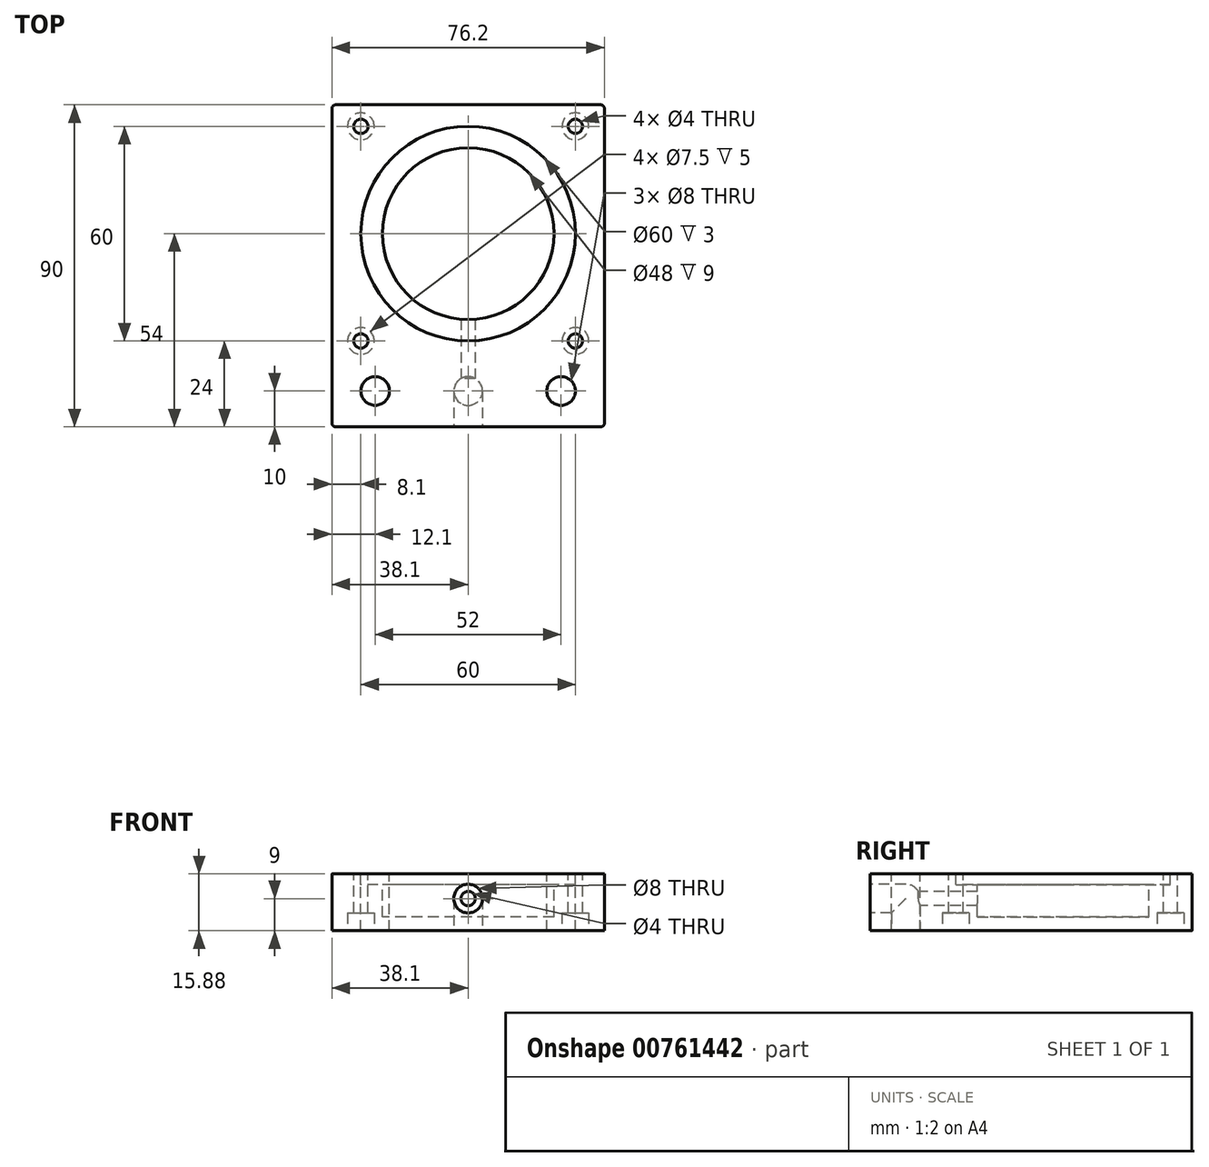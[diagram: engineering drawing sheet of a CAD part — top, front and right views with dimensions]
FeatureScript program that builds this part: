
annotation { "Feature Type Name" : "Feature", "Feature Type Description" : "" }
export const myFeature = defineFeature(function(context is Context, id is Id, definition is map)
    precondition{}
    {
        {
            var Q0;
            Q0=qCreatedBy(makeId("Top.planeOp"),FACE);
            var sketch = newSketch(context, id + "F0", { "sketchPlane" : qUnion([Q0])});
            skLineSegment(sketch, "E0.bottom", {"start": v(0, 0) * mm, "end": v(76.2, 0) * mm});
            skLineSegment(sketch, "E0.top", {"start": v(0, 90) * mm, "end": v(76.2, 90) * mm});
            skLineSegment(sketch, "E0.left", {"start": v(0, 0) * mm, "end": v(0, 90) * mm});
            skLineSegment(sketch, "E0.right", {"start": v(76.2, 0) * mm, "end": v(76.2, 90) * mm});
            skSolve(sketch);
        }
        {
            var Q0;
            Q0=makeQuery(id+"F0.imprint","IMPRINT",FACE,{"disambiguationData":[TD([[makeQuery(id+"F0.imprint","IMPRINT",EDGE,{"derivedFrom":sQuery(id+"F0.wireOp",EDGE,"E0.bottom")}),1.0]])]});
            extrude(context, id + "F1", {"entities" : qUnion([Q0]), "depth" : 15.88 * mm, "offsetDistance" : 25 * mm});
        }
        {
            var Q0;
            Q0=makeQuery(id+"F1.opExtrude","CAP_FACE",FACE,{"disambiguationData":[OSD([sQuery(id+"F0.wireOp",EDGE,"E0.bottom"),sQuery(id+"F0.wireOp",EDGE,"E0.top"),sQuery(id+"F0.wireOp",EDGE,"E0.left"),sQuery(id+"F0.wireOp",EDGE,"E0.right")])],"isStart":false});
            var sketch = newSketch(context, id + "F2", { "sketchPlane" : qUnion([Q0])});
            skCircle(sketch, "E1", {"center": v(38.1, 54) * mm, "radius": 24 * mm});
            skSolve(sketch);
        }
        {
            var Q0;
            Q0=makeQuery(id+"F2.imprint","IMPRINT",FACE,{"disambiguationData":[TD([[makeQuery(id+"F2.imprint","IMPRINT",EDGE,{"derivedFrom":sQuery(id+"F2.wireOp",EDGE,"E1")}),1.0]])]});
            extrude(context, id + "F3", {"entities" : qUnion([Q0]), "operationType" : NewBodyOperationType.REMOVE, "oppositeDirection" : true, "depth" : 12 * mm, "offsetDistance" : 25 * mm});
        }
        {
            var Q0;
            Q0=makeQuery(id+"F1.opExtrude","CAP_FACE",FACE,{"disambiguationData":[OSD([sQuery(id+"F0.wireOp",EDGE,"E0.bottom"),sQuery(id+"F0.wireOp",EDGE,"E0.top"),sQuery(id+"F0.wireOp",EDGE,"E0.left"),sQuery(id+"F0.wireOp",EDGE,"E0.right")])],"isStart":false});
            var sketch = newSketch(context, id + "F4", { "sketchPlane" : qUnion([Q0])});
            skCircle(sketch, "E2", {"center": v(38.1, 54) * mm, "radius": 30 * mm});
            skSolve(sketch);
        }
        {
            var Q0;
            Q0=makeQuery(id+"F4.imprint","IMPRINT",FACE,{"disambiguationData":[TD([[makeQuery(id+"F4.imprint","IMPRINT",EDGE,{"derivedFrom":sQuery(id+"F4.wireOp",EDGE,"E2")}),1.0]])]});
            var Q1;
            Q1=sQuery(id+"F4.wireOp",EDGE,"E2");
            extrude(context, id + "F5", {"entities" : qUnion([Q0]), "operationType" : NewBodyOperationType.REMOVE, "surfaceEntities" : qUnion([Q1]), "oppositeDirection" : true, "depth" : 3 * mm, "offsetDistance" : 25 * mm});
        }
        {
            var Q0;
            Q0=makeQuery(id+"F1.opExtrude","SWEPT_FACE",FACE,{"disambiguationData":[OSD([sQuery(id+"F0.wireOp",EDGE,"E0.bottom")])]});
            var sketch = newSketch(context, id + "F6", { "sketchPlane" : qUnion([Q0])});
            skCircle(sketch, "E3", {"center": v(38.1, 9) * mm, "radius": 4 * mm});
            skSolve(sketch);
        }
        {
            var Q0;
            Q0=makeQuery(id+"F6.imprint","IMPRINT",FACE,{"disambiguationData":[TD([[makeQuery(id+"F6.imprint","IMPRINT",EDGE,{"derivedFrom":sQuery(id+"F6.wireOp",EDGE,"E3")}),1.0]])]});
            extrude(context, id + "F7", {"entities" : qUnion([Q0]), "operationType" : NewBodyOperationType.REMOVE, "oppositeDirection" : true, "depth" : 10 * mm, "offsetDistance" : 25 * mm});
        }
        {
            var Q0;
            Q0=makeQuery(id+"F1.opExtrude","CAP_FACE",FACE,{"disambiguationData":[OSD([sQuery(id+"F0.wireOp",EDGE,"E0.bottom"),sQuery(id+"F0.wireOp",EDGE,"E0.top"),sQuery(id+"F0.wireOp",EDGE,"E0.left"),sQuery(id+"F0.wireOp",EDGE,"E0.right")])],"isStart":true});
            var sketch = newSketch(context, id + "F8", { "sketchPlane" : qUnion([Q0])});
            skCircle(sketch, "E4", {"center": v(38.1, -10) * mm, "radius": 4 * mm});
            skSolve(sketch);
        }
        {
            var Q0;
            Q0=makeQuery(id+"F8.imprint","IMPRINT",FACE,{"disambiguationData":[TD([[makeQuery(id+"F8.imprint","IMPRINT",EDGE,{"derivedFrom":sQuery(id+"F8.wireOp",EDGE,"E4")}),1.0]])]});
            extrude(context, id + "F9", {"entities" : qUnion([Q0]), "operationType" : NewBodyOperationType.REMOVE, "oppositeDirection" : true, "depth" : 9 * mm, "offsetDistance" : 25 * mm});
        }
        {
            var Q0;
            Q0=makeQuery(id+"F7.boolean.opBoolean","COPY",FACE,{"derivedFrom":makeQuery(id+"F7.opExtrude","CAP_FACE",FACE,{"disambiguationData":[OSD([sQuery(id+"F6.wireOp",EDGE,"E3")])],"isStart":false})});
            var sketch = newSketch(context, id + "F10", { "sketchPlane" : qUnion([Q0])});
            skArc(sketch, "E5", {"start": v(38.1, 13) * mm, "mid": v(34.1, 9) * mm, "end": v(38.1, 5) * mm});
            skLineSegment(sketch, "E6", {"start": v(38.1, 13) * mm, "end": v(38.1, 5) * mm});
            skSolve(sketch);
        }
        {
            var Q0;
            {var subQ0=sQuery(id+"F10.wireOp",EDGE,"E5");var subQ1=sQuery(id+"F6.wireOp",EDGE,"E3");var subQ2=makeQuery(id+"F9.boolean.opBoolean","INTERSECT",EDGE,{"derivedFrom":[makeQuery(id+"F7.boolean.opBoolean","COPY",FACE,{"derivedFrom":makeQuery(id+"F7.opExtrude","CAP_FACE",FACE,{"disambiguationData":[OSD([subQ1])],"isStart":false})}),makeQuery(id+"F9.opExtrude","CAP_FACE",FACE,{"disambiguationData":[OSD([sQuery(id+"F8.wireOp",EDGE,"E4")])],"isStart":false})]});var subQ3=makeQuery(id+"F10.imprint","INTERSECT",VERTEX,{"derivedFrom":[subQ2,subQ0]});Q0=makeQuery(id+"F10.imprint","IMPRINT",FACE,{"disambiguationData":[TD([[makeQuery(id+"F10.imprint","IMPRINT",EDGE,{"disambiguationData":[TD([[subQ3,1.0]])],"derivedFrom":subQ0}),1.0]])]});}
            var Q1;
            Q1=sQuery(id+"F10.wireOp",EDGE,"E6");
            revolve(context, id + "F11", {"operationType" : NewBodyOperationType.REMOVE, "surfaceOperationType" : NewSurfaceOperationType.NEW, "entities" : qUnion([Q0]), "axis" : qUnion([Q1]), "revolveType" : RevolveType.FULL, "oppositeDirection" : true});
        }
        {
            var Q0;
            Q0=makeQuery(id+"F1.opExtrude","SWEPT_FACE",FACE,{"disambiguationData":[OSD([sQuery(id+"F0.wireOp",EDGE,"E0.bottom")])]});
            var sketch = newSketch(context, id + "F12", { "sketchPlane" : qUnion([Q0])});
            skCircle(sketch, "E7", {"center": v(38.1, 9) * mm, "radius": 2 * mm});
            skSolve(sketch);
        }
        {
            var Q0;
            Q0=makeQuery(id+"F12.imprint","IMPRINT",FACE,{"disambiguationData":[TD([[makeQuery(id+"F12.imprint","IMPRINT",EDGE,{"derivedFrom":sQuery(id+"F12.wireOp",EDGE,"E7")}),1.0]])]});
            extrude(context, id + "F13", {"entities" : qUnion([Q0]), "operationType" : NewBodyOperationType.REMOVE, "oppositeDirection" : true, "depth" : 50 * mm, "offsetDistance" : 25 * mm});
        }
        {
            var Q0;
            Q0=makeQuery(id+"F5.boolean.opBoolean","COPY",EDGE,{"derivedFrom":makeQuery(id+"F5.opExtrude","CAP_EDGE",EDGE,{"disambiguationData":[OSD([sQuery(id+"F2.wireOp",EDGE,"E1")])],"isStart":false})});
            var Q1;
            Q1=makeQuery(id+"F1.opExtrude","SWEPT_EDGE",EDGE,{"disambiguationData":[OSD([sQuery(id+"F0.wireOp",EDGE,"E0.top"),sQuery(id+"F0.wireOp",EDGE,"E0.left")])]});
            var Q2;
            Q2=makeQuery(id+"F1.opExtrude","SWEPT_EDGE",EDGE,{"disambiguationData":[OSD([sQuery(id+"F0.wireOp",EDGE,"E0.bottom"),sQuery(id+"F0.wireOp",EDGE,"E0.left")])]});
            var Q3;
            Q3=makeQuery(id+"F1.opExtrude","SWEPT_EDGE",EDGE,{"disambiguationData":[OSD([sQuery(id+"F0.wireOp",EDGE,"E0.top"),sQuery(id+"F0.wireOp",EDGE,"E0.right")])]});
            var Q4;
            Q4=makeQuery(id+"F1.opExtrude","SWEPT_EDGE",EDGE,{"disambiguationData":[OSD([sQuery(id+"F0.wireOp",EDGE,"E0.bottom"),sQuery(id+"F0.wireOp",EDGE,"E0.right")])]});
            fillet(context, id + "F14", {"entities" : qUnion([Q0, Q1, Q2, Q3, Q4]), "radius" : 1 * mm, "tangentPropagation" : true, "allowEdgeOverflow" : false});
        }
        {
            var Q0;
            Q0=makeQuery(id+"F1.opExtrude","CAP_FACE",FACE,{"disambiguationData":[OSD([sQuery(id+"F0.wireOp",EDGE,"E0.bottom"),sQuery(id+"F0.wireOp",EDGE,"E0.top"),sQuery(id+"F0.wireOp",EDGE,"E0.left"),sQuery(id+"F0.wireOp",EDGE,"E0.right")])],"isStart":false});
            var sketch = newSketch(context, id + "F15", { "sketchPlane" : qUnion([Q0])});
            skCircle(sketch, "E8", {"center": v(8.1, 84) * mm, "radius": 2 * mm});
            skCircle(sketch, "E9", {"center": v(68.1, 84) * mm, "radius": 2 * mm});
            skCircle(sketch, "E10", {"center": v(8.1, 24) * mm, "radius": 2 * mm});
            skCircle(sketch, "E11", {"center": v(68.1, 24) * mm, "radius": 2 * mm});
            skCircle(sketch, "E12", {"center": v(12.1, 10) * mm, "radius": 4 * mm});
            skCircle(sketch, "E13", {"center": v(64.1, 10) * mm, "radius": 4 * mm});
            skSolve(sketch);
        }
        {
            var Q0;
            Q0 = qSketchRegion(id + "F15", true);
            extrude(context, id + "F16", {"entities" : qUnion([Q0]), "operationType" : NewBodyOperationType.REMOVE, "oppositeDirection" : true, "depth" : 16 * mm, "offsetDistance" : 25 * mm});
        }
        {
            var Q0;
            Q0=makeQuery(id+"F1.opExtrude","CAP_FACE",FACE,{"disambiguationData":[OSD([sQuery(id+"F0.wireOp",EDGE,"E0.bottom"),sQuery(id+"F0.wireOp",EDGE,"E0.top"),sQuery(id+"F0.wireOp",EDGE,"E0.left"),sQuery(id+"F0.wireOp",EDGE,"E0.right")])],"isStart":true});
            var sketch = newSketch(context, id + "F17", { "sketchPlane" : qUnion([Q0])});
            skCircle(sketch, "E14", {"center": v(8.1, -24) * mm, "radius": 3.75 * mm});
            skCircle(sketch, "E15", {"center": v(68.1, -24) * mm, "radius": 3.75 * mm});
            skCircle(sketch, "E16", {"center": v(8.1, -84) * mm, "radius": 3.75 * mm});
            skCircle(sketch, "E17", {"center": v(68.1, -84) * mm, "radius": 3.75 * mm});
            skSolve(sketch);
        }
        {
            var Q0;
            Q0 = qSketchRegion(id + "F17", true);
            extrude(context, id + "F18", {"entities" : qUnion([Q0]), "operationType" : NewBodyOperationType.REMOVE, "oppositeDirection" : true, "depth" : 5 * mm, "offsetDistance" : 25 * mm});
        }
    });
